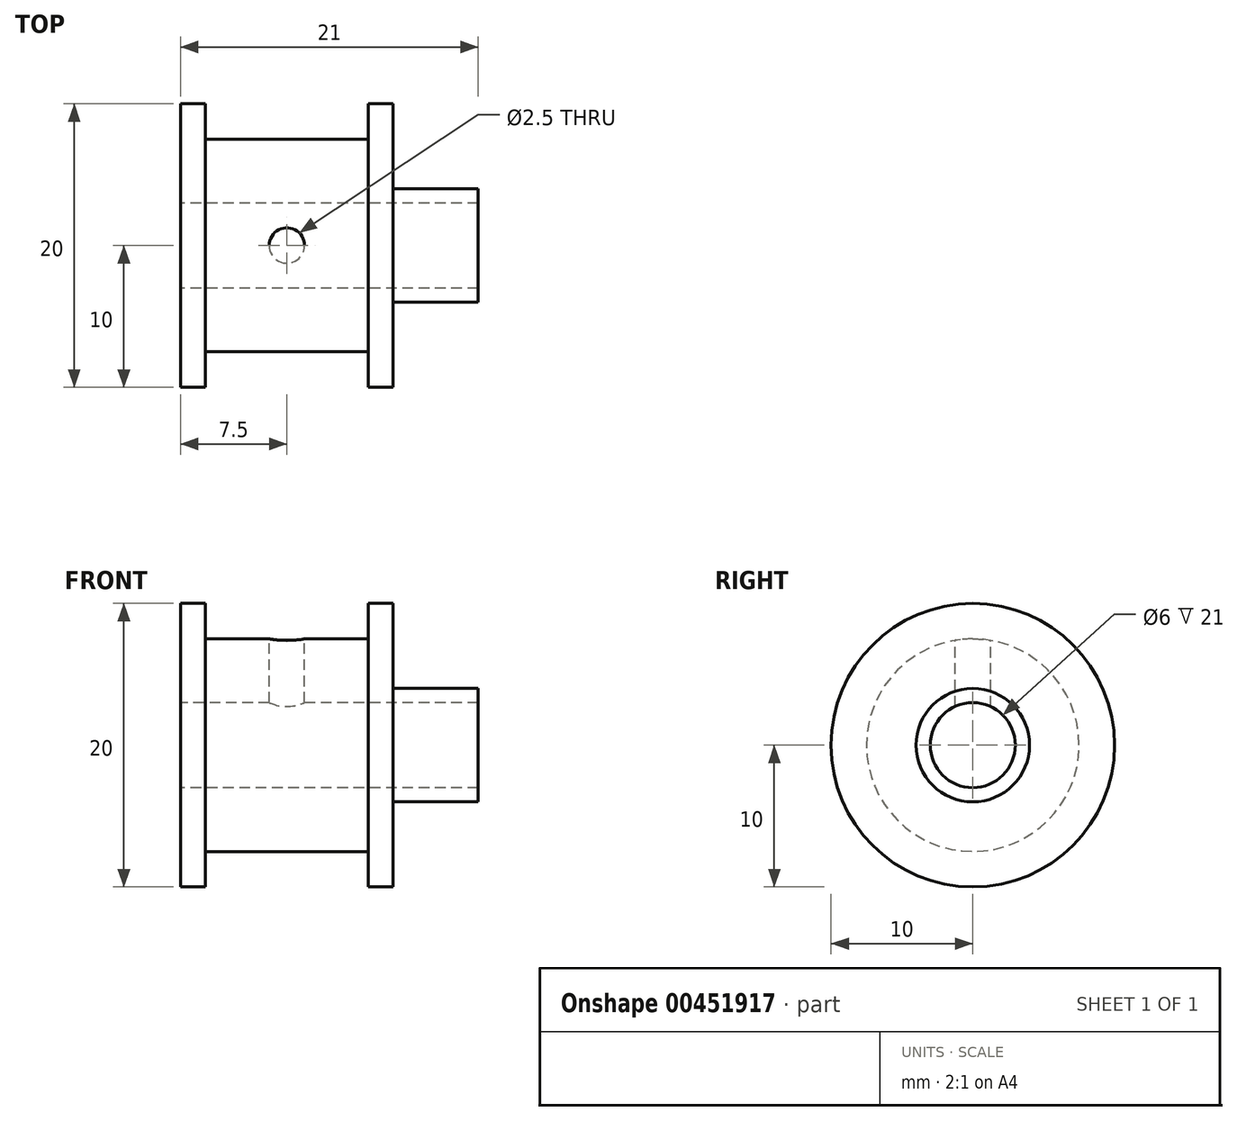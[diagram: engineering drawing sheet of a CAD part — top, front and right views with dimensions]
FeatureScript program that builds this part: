
annotation { "Feature Type Name" : "Feature", "Feature Type Description" : "" }
export const myFeature = defineFeature(function(context is Context, id is Id, definition is map)
    precondition{}
    {
        {
            var Q0;
            Q0=qCreatedBy(makeId("Front.planeOp"),FACE);
            var sketch = newSketch(context, id + "F0", { "sketchPlane" : qUnion([Q0])});
            skLineSegment(sketch, "E0", {"start": v(-18.22, 0) * mm, "end": v(20.5, 0) * mm, "construction": true});
            skLineSegment(sketch, "E1", {"start": v(13.5, 3) * mm, "end": v(-7.5, 3) * mm});
            skLineSegment(sketch, "E2", {"start": v(-7.5, 3) * mm, "end": v(-7.5, 10) * mm});
            skLineSegment(sketch, "E3", {"start": v(-7.5, 10) * mm, "end": v(-5.75, 10) * mm});
            skLineSegment(sketch, "E4", {"start": v(-5.75, 10) * mm, "end": v(-5.75, 7.5) * mm});
            skLineSegment(sketch, "E5", {"start": v(-5.75, 7.5) * mm, "end": v(5.75, 7.5) * mm});
            skLineSegment(sketch, "E6", {"start": v(5.75, 7.5) * mm, "end": v(5.75, 10) * mm});
            skLineSegment(sketch, "E7", {"start": v(5.75, 10) * mm, "end": v(7.5, 10) * mm});
            skLineSegment(sketch, "E8", {"start": v(7.5, 10) * mm, "end": v(7.5, 4) * mm});
            skLineSegment(sketch, "E9", {"start": v(7.5, 4) * mm, "end": v(13.5, 4) * mm});
            skLineSegment(sketch, "E10", {"start": v(13.5, 4) * mm, "end": v(13.5, 3) * mm});
            skPoint(sketch, "E11", {"position": v(0, 7.5) * mm});
            skSolve(sketch);
        }
        {
            var Q0;
            Q0=qSketchRegion(id+"F0",true);
            var Q1;
            Q1=sQuery(id+"F0.wireOp",EDGE,"E0");
            revolve(context, id + "F1", {"entities" : qUnion([Q0]), "axis" : qUnion([Q1]), "revolveType" : RevolveType.FULL});
        }
        {
            var Q0;
            Q0=qCreatedBy(makeId("Top.planeOp"),FACE);
            cPlane(context, id + "F2", {"entities" : qUnion([Q0]), "cplaneType" : CPlaneType.OFFSET, "offset" : 25 * mm, "width" : 150 * mm, "height" : 150 * mm});
        }
        {
            var Q0;
            Q0=qCreatedBy(id+"F2.planeOp",FACE);
            var sketch = newSketch(context, id + "F3", { "sketchPlane" : qUnion([Q0])});
            skPoint(sketch, "E12", {"position": v(0, 0) * mm});
            skSolve(sketch);
        }
        {
            var Q0;
            Q0=sQuery(id+"F3.wireOp",VERTEX,"E12");
            var Q1;
            Q1=makeQuery(id+"F1.opRevolve","SWEPT_BODY",BODY,{"disambiguationData":[OSD([sQuery(id+"F0.wireOp",EDGE,"E1"),sQuery(id+"F0.wireOp",EDGE,"E2"),sQuery(id+"F0.wireOp",EDGE,"E3"),sQuery(id+"F0.wireOp",EDGE,"E4"),sQuery(id+"F0.wireOp",EDGE,"E5"),sQuery(id+"F0.wireOp",EDGE,"E6"),sQuery(id+"F0.wireOp",EDGE,"E7"),sQuery(id+"F0.wireOp",EDGE,"E8"),sQuery(id+"F0.wireOp",EDGE,"E9"),sQuery(id+"F0.wireOp",EDGE,"E10")])]});
            hole(context, id + "F4", {"style" : HoleStyle.SIMPLE, "endStyle" : HoleEndStyle.BLIND, "standardTappedOrClearance" : lookupTablePath({ "standard" : "ISO", "engagement" : "75%", "pitch" : "0.5 mm", "size" : "M3", "type" : "Tapped" }), "standardBlindInLast" : lookupTablePath({ "standard" : "ISO", "engagement" : "75%", "pitch" : "0.5 mm", "size" : "M3", "type" : "Tapped" }), "holeDiameter" : 2.5 * mm, "showTappedDepth" : true, "holeDepth" : 8 * mm, "tappedDepth" : 6.5 * mm, "tapClearance" : 3, "locations" : qUnion([Q0]), "scope" : qUnion([Q1]), "majorDiameter" : 3 * mm});
        }
    });
